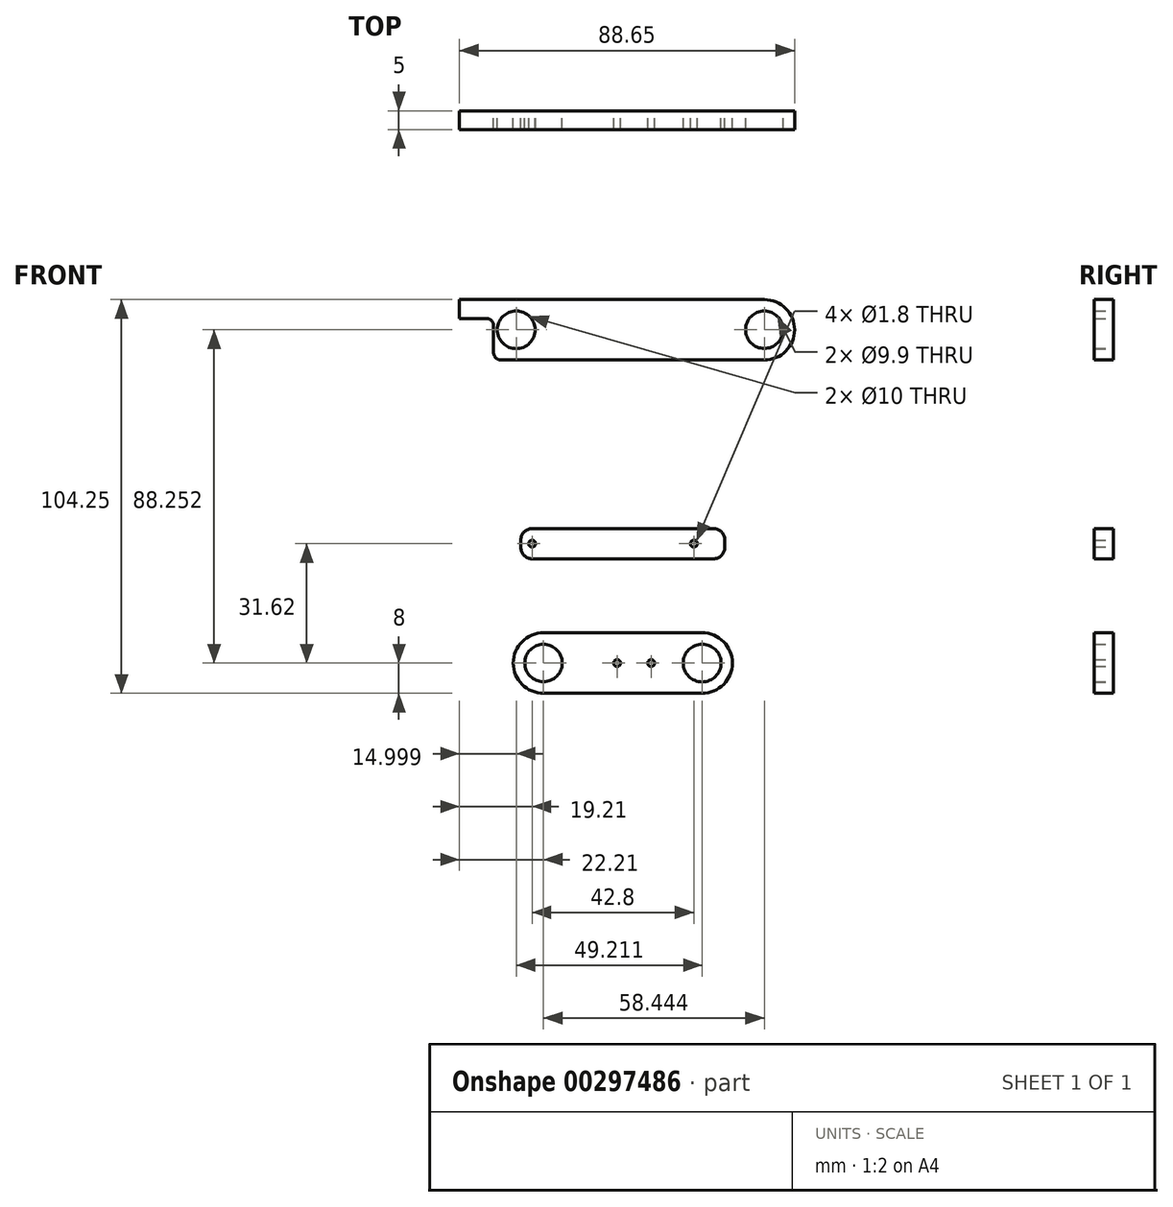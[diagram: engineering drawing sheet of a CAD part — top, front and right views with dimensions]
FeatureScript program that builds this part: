
annotation { "Feature Type Name" : "Feature", "Feature Type Description" : "" }
export const myFeature = defineFeature(function(context is Context, id is Id, definition is map)
    precondition{}
    {
        {
            var Q0;
            Q0=qCreatedBy(makeId("Front.planeOp"),FACE);
            var sketch = newSketch(context, id + "F0", { "sketchPlane" : qUnion([Q0])});
            skPoint(sketch, "E0", {"position": v(-74.78, 0) * mm});
            skPoint(sketch, "E1", {"position": v(0, 0) * mm});
            skPoint(sketch, "E2", {"position": v(8.7, -18.18) * mm});
            skPoint(sketch, "E3", {"position": v(11.78, -63.82) * mm});
            skPoint(sketch, "E4", {"position": v(-71.78, -13) * mm});
            skLineSegment(sketch, "E5", {"start": v(-71.78, -13) * mm, "end": v(8.7, -18.18) * mm});
            skLineSegment(sketch, "E6", {"start": v(-56.81, -13.96) * mm, "end": v(11.78, -63.82) * mm});
            skLineSegment(sketch, "E7.bottom", {"start": v(37.44, 126.92) * mm, "end": v(-32.21, 126.92) * mm});
            skLineSegment(sketch, "E7.top", {"start": v(37.44, 142.92) * mm, "end": v(-32.21, 142.92) * mm});
            skLineSegment(sketch, "E7.left", {"start": v(45.44, 134.92) * mm, "end": v(45.44, 134.92) * mm});
            skPoint(sketch, "E7.middle", {"position": v(0, 134.92) * mm});
            skCircle(sketch, "E8", {"center": v(37.44, 134.92) * mm, "radius": 4.95 * mm});
            skPoint(sketch, "E8.centerSnap0", {"position": v(45.44, 134.92) * mm});
            skLineSegment(sketch, "E9.bottom", {"start": v(24, 74.3) * mm, "end": v(-24, 74.3) * mm});
            skLineSegment(sketch, "E9.top", {"start": v(24, 82.3) * mm, "end": v(-24, 82.3) * mm});
            skLineSegment(sketch, "E9.left", {"start": v(27, 77.3) * mm, "end": v(27, 79.3) * mm});
            skLineSegment(sketch, "E9.right", {"start": v(-27, 77.3) * mm, "end": v(-27, 79.3) * mm});
            skPoint(sketch, "E9.middle", {"position": v(0, 78.3) * mm});
            skLineSegment(sketch, "E10.bottom", {"start": v(21, 38.67) * mm, "end": v(-21, 38.67) * mm});
            skLineSegment(sketch, "E10.top", {"start": v(21, 54.67) * mm, "end": v(-21, 54.67) * mm});
            skLineSegment(sketch, "E10.left", {"start": v(29, 46.67) * mm, "end": v(29, 46.67) * mm});
            skLineSegment(sketch, "E10.right", {"start": v(-29, 46.67) * mm, "end": v(-29, 46.67) * mm});
            skPoint(sketch, "E10.middle", {"position": v(0, 46.67) * mm});
            skCircle(sketch, "E11", {"center": v(-24, 78.3) * mm, "radius": 0.9 * mm});
            skPoint(sketch, "E11.centerSnap0", {"position": v(-27, 78.3) * mm});
            skCircle(sketch, "E12", {"center": v(18.8, 78.3) * mm, "radius": 0.9 * mm});
            skPoint(sketch, "E12.centerSnap0", {"position": v(27, 78.3) * mm});
            skCircle(sketch, "E13", {"center": v(-21, 46.67) * mm, "radius": 4.95 * mm});
            skPoint(sketch, "E14", {"position": v(21, 46.67) * mm});
            skCircle(sketch, "E15.1.0", {"center": v(7.5, 46.67) * mm, "radius": 0.9 * mm});
            skCircle(sketch, "E15.1.1", {"center": v(-1.5, 46.67) * mm, "radius": 0.9 * mm});
            skCircle(sketch, "E16", {"center": v(-28.21, 134.92) * mm, "radius": 5 * mm});
            skLineSegment(sketch, "E17", {"start": v(-43.21, 137.92) * mm, "end": v(-36.21, 137.92) * mm});
            skLineSegment(sketch, "E18", {"start": v(-34.21, 135.92) * mm, "end": v(-34.21, 128.92) * mm});
            skPoint(sketch, "E19.visualSharp", {"position": v(-34.21, 137.92) * mm});
            skArc(sketch, "E19.filletArc", {"start": v(-34.21, 135.92) * mm, "mid": v(-34.8, 137.34) * mm, "end": v(-36.21, 137.92) * mm});
            skCircle(sketch, "E20", {"center": v(21, 46.67) * mm, "radius": 5 * mm});
            skPoint(sketch, "E21.visualSharp", {"position": v(45.44, 142.92) * mm});
            skArc(sketch, "E21.filletArc", {"start": v(45.44, 134.92) * mm, "mid": v(43.1, 140.58) * mm, "end": v(37.44, 142.92) * mm});
            skPoint(sketch, "E22.visualSharp", {"position": v(45.44, 126.92) * mm});
            skArc(sketch, "E22.filletArc", {"start": v(37.44, 126.92) * mm, "mid": v(43.1, 129.27) * mm, "end": v(45.44, 134.92) * mm});
            skPoint(sketch, "E23.visualSharp", {"position": v(-34.21, 126.92) * mm});
            skArc(sketch, "E23.filletArc", {"start": v(-34.21, 128.92) * mm, "mid": v(-33.62, 127.5) * mm, "end": v(-32.21, 126.92) * mm});
            skPoint(sketch, "E24.visualSharp", {"position": v(-27, 82.3) * mm});
            skArc(sketch, "E24.filletArc", {"start": v(-24, 82.3) * mm, "mid": v(-26.12, 81.41) * mm, "end": v(-27, 79.3) * mm});
            skPoint(sketch, "E25.visualSharp", {"position": v(-27, 74.3) * mm});
            skArc(sketch, "E25.filletArc", {"start": v(-27, 77.3) * mm, "mid": v(-26.12, 75.17) * mm, "end": v(-24, 74.3) * mm});
            skPoint(sketch, "E26.visualSharp", {"position": v(27, 74.3) * mm});
            skArc(sketch, "E26.filletArc", {"start": v(24, 74.3) * mm, "mid": v(26.12, 75.17) * mm, "end": v(27, 77.3) * mm});
            skPoint(sketch, "E27.visualSharp", {"position": v(27, 82.3) * mm});
            skArc(sketch, "E27.filletArc", {"start": v(27, 79.3) * mm, "mid": v(26.12, 81.41) * mm, "end": v(24, 82.3) * mm});
            skPoint(sketch, "E28.visualSharp", {"position": v(-29, 54.67) * mm});
            skArc(sketch, "E28.filletArc", {"start": v(-21, 54.67) * mm, "mid": v(-26.66, 52.33) * mm, "end": v(-29, 46.67) * mm});
            skPoint(sketch, "E29.visualSharp", {"position": v(-29, 38.67) * mm});
            skArc(sketch, "E29.filletArc", {"start": v(-29, 46.67) * mm, "mid": v(-26.66, 41.01) * mm, "end": v(-21, 38.67) * mm});
            skPoint(sketch, "E30.visualSharp", {"position": v(29, 54.67) * mm});
            skArc(sketch, "E30.filletArc", {"start": v(29, 46.67) * mm, "mid": v(26.66, 52.33) * mm, "end": v(21, 54.67) * mm});
            skPoint(sketch, "E31.visualSharp", {"position": v(29, 38.67) * mm});
            skArc(sketch, "E31.filletArc", {"start": v(21, 38.67) * mm, "mid": v(26.66, 41.01) * mm, "end": v(29, 46.67) * mm});
            skLineSegment(sketch, "E32", {"start": v(-32.21, 142.92) * mm, "end": v(-43.21, 142.92) * mm});
            skLineSegment(sketch, "E33", {"start": v(-43.21, 137.92) * mm, "end": v(-43.21, 142.92) * mm});
            skSolve(sketch);
        }
        {
            var Q0;
            Q0=makeQuery(id+"F0.imprint","IMPRINT",FACE,{"disambiguationData":[TD([[makeQuery(id+"F0.imprint","IMPRINT",EDGE,{"derivedFrom":sQuery(id+"F0.wireOp",EDGE,"E7.bottom")}),-1.0]])]});
            var Q1;
            Q1=makeQuery(id+"F0.imprint","IMPRINT",FACE,{"disambiguationData":[TD([[makeQuery(id+"F0.imprint","IMPRINT",EDGE,{"derivedFrom":sQuery(id+"F0.wireOp",EDGE,"E9.bottom")}),-1.0]])]});
            var Q2;
            Q2=makeQuery(id+"F0.imprint","IMPRINT",FACE,{"disambiguationData":[TD([[makeQuery(id+"F0.imprint","IMPRINT",EDGE,{"derivedFrom":sQuery(id+"F0.wireOp",EDGE,"E10.bottom")}),-1.0]])]});
            extrude(context, id + "F1", {"entities" : qUnion([Q0, Q1, Q2]), "depth" : 5 * mm});
        }
    });
